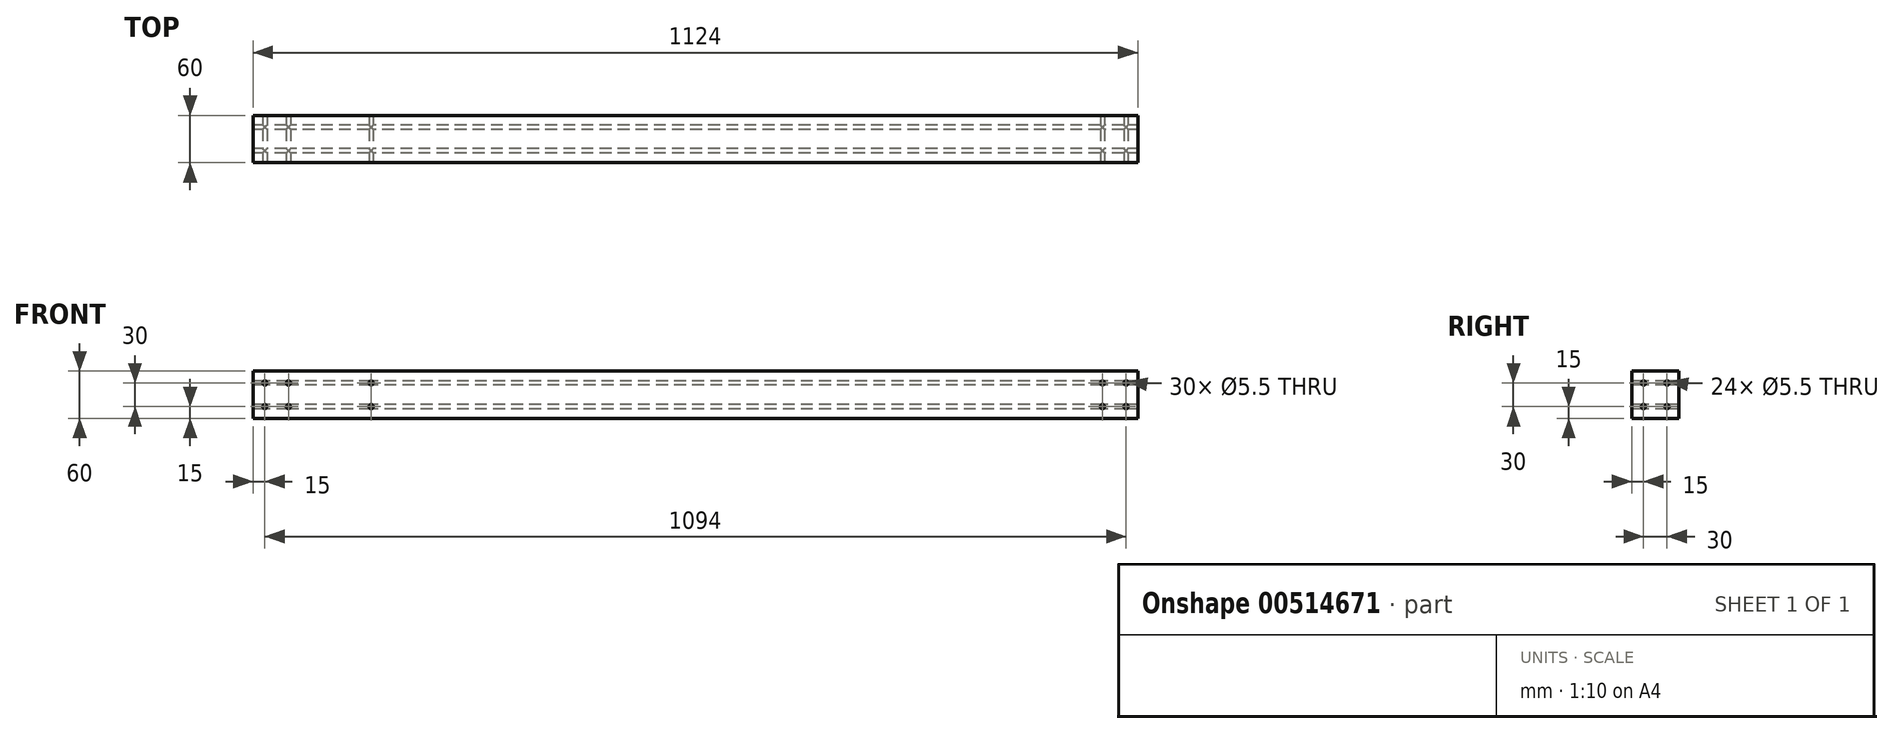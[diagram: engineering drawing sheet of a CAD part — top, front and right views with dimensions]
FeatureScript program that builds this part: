
annotation { "Feature Type Name" : "Feature", "Feature Type Description" : "" }
export const myFeature = defineFeature(function(context is Context, id is Id, definition is map)
    precondition{}
    {
        {
            var Q0;
            Q0=qCreatedBy(makeId("Right.planeOp"),FACE);
            var sketch = newSketch(context, id + "F0", { "sketchPlane" : qUnion([Q0])});
            skLineSegment(sketch, "E0.bottom", {"start": v(0, 0) * mm, "end": v(-60, 0) * mm});
            skLineSegment(sketch, "E0.top", {"start": v(0, 60) * mm, "end": v(-60, 60) * mm});
            skLineSegment(sketch, "E0.left", {"start": v(0, 0) * mm, "end": v(0, 60) * mm});
            skLineSegment(sketch, "E0.right", {"start": v(-60, 0) * mm, "end": v(-60, 60) * mm});
            skPoint(sketch, "E1", {"position": v(-45, 45) * mm});
            skPoint(sketch, "E2", {"position": v(-45, 15) * mm});
            skPoint(sketch, "E3", {"position": v(-15, 15) * mm});
            skPoint(sketch, "E4", {"position": v(-15, 45) * mm});
            skSolve(sketch);
        }
        {
            var Q0;
            Q0=makeQuery(id+"F0.imprint","IMPRINT",FACE,{"disambiguationData":[TD([[makeQuery(id+"F0.imprint","IMPRINT",EDGE,{"derivedFrom":sQuery(id+"F0.wireOp",EDGE,"E0.bottom")}),-1.0]])]});
            extrude(context, id + "F1", {"entities" : qUnion([Q0]), "depth" : 1124 * mm, "offsetDistance" : 25 * mm});
        }
        {
            var Q0;
            Q0=sQuery(id+"F0.wireOp",VERTEX,"E1");
            var Q1;
            Q1=sQuery(id+"F0.wireOp",VERTEX,"E2");
            var Q2;
            Q2=sQuery(id+"F0.wireOp",VERTEX,"E3");
            var Q3;
            Q3=sQuery(id+"F0.wireOp",VERTEX,"E4");
            var Q4;
            Q4=makeQuery(id+"F1.opExtrude","SWEPT_BODY",BODY,{"disambiguationData":[OSD([sQuery(id+"F0.wireOp",EDGE,"E0.bottom"),sQuery(id+"F0.wireOp",EDGE,"E0.top"),sQuery(id+"F0.wireOp",EDGE,"E0.left"),sQuery(id+"F0.wireOp",EDGE,"E0.right")])]});
            hole(context, id + "F2", {"style" : HoleStyle.SIMPLE, "endStyle" : HoleEndStyle.THROUGH, "oppositeDirection" : true, "standardTappedOrClearance" : lookupTablePath({ "standard" : "ISO", "fit" : "Normal", "size" : "M5", "type" : "Clearance" }), "standardBlindInLast" : lookupTablePath({ "fit" : "Standard", "standard" : "ISO", "size" : "M5", "type" : "Clearance" }), "holeDiameter" : 5.5 * mm, "isTappedThrough" : true, "tappedDepth" : 12 * mm, "tapClearance" : 3, "locations" : qUnion([Q0, Q1, Q2, Q3]), "scope" : qUnion([Q4])});
        }
        {
            var Q0;
            Q0=makeQuery(id+"F1.opExtrude","SWEPT_FACE",FACE,{"disambiguationData":[OSD([sQuery(id+"F0.wireOp",EDGE,"E0.right")])]});
            var sketch = newSketch(context, id + "F3", { "sketchPlane" : qUnion([Q0])});
            skPoint(sketch, "E5", {"position": v(150, 45) * mm});
            skPoint(sketch, "E6", {"position": v(150, 15) * mm});
            skPoint(sketch, "E7", {"position": v(15, 45) * mm});
            skPoint(sketch, "E8", {"position": v(45, 45) * mm});
            skPoint(sketch, "E9", {"position": v(45, 15) * mm});
            skPoint(sketch, "E10", {"position": v(15, 15) * mm});
            skPoint(sketch, "E11", {"position": v(1079, 45) * mm});
            skPoint(sketch, "E12", {"position": v(1109, 45) * mm});
            skPoint(sketch, "E13", {"position": v(1109, 15) * mm});
            skPoint(sketch, "E14", {"position": v(1079, 15) * mm});
            skSolve(sketch);
        }
        {
            var Q0;
            Q0=sQuery(id+"F3.wireOp",VERTEX,"E5");
            var Q1;
            Q1=sQuery(id+"F3.wireOp",VERTEX,"E6");
            var Q2;
            Q2=makeQuery(id+"F1.opExtrude","SWEPT_BODY",BODY,{"disambiguationData":[OSD([sQuery(id+"F0.wireOp",EDGE,"E0.bottom"),sQuery(id+"F0.wireOp",EDGE,"E0.top"),sQuery(id+"F0.wireOp",EDGE,"E0.left"),sQuery(id+"F0.wireOp",EDGE,"E0.right")])]});
            hole(context, id + "F4", {"style" : HoleStyle.SIMPLE, "endStyle" : HoleEndStyle.THROUGH, "standardTappedOrClearance" : lookupTablePath({ "standard" : "ISO", "fit" : "Normal", "size" : "M5", "type" : "Clearance" }), "standardBlindInLast" : lookupTablePath({ "fit" : "Standard", "standard" : "ISO", "size" : "M5", "type" : "Clearance" }), "holeDiameter" : 5.5 * mm, "isTappedThrough" : true, "tappedDepth" : 12 * mm, "tapClearance" : 3, "locations" : qUnion([Q0, Q1]), "scope" : qUnion([Q2])});
        }
        {
            var Q0;
            Q0=sQuery(id+"F3.wireOp",VERTEX,"E8");
            var Q1;
            Q1=sQuery(id+"F3.wireOp",VERTEX,"E7");
            var Q2;
            Q2=sQuery(id+"F3.wireOp",VERTEX,"E10");
            var Q3;
            Q3=sQuery(id+"F3.wireOp",VERTEX,"E9");
            var Q4;
            Q4=sQuery(id+"F3.wireOp",VERTEX,"E12");
            var Q5;
            Q5=sQuery(id+"F3.wireOp",VERTEX,"E14");
            var Q6;
            Q6=sQuery(id+"F3.wireOp",VERTEX,"E13");
            var Q7;
            Q7=sQuery(id+"F3.wireOp",VERTEX,"E11");
            var Q8;
            Q8=makeQuery(id+"F1.opExtrude","SWEPT_BODY",BODY,{"disambiguationData":[OSD([sQuery(id+"F0.wireOp",EDGE,"E0.bottom"),sQuery(id+"F0.wireOp",EDGE,"E0.top"),sQuery(id+"F0.wireOp",EDGE,"E0.left"),sQuery(id+"F0.wireOp",EDGE,"E0.right")])]});
            hole(context, id + "F5", {"style" : HoleStyle.SIMPLE, "endStyle" : HoleEndStyle.THROUGH, "standardTappedOrClearance" : lookupTablePath({ "standard" : "ISO", "fit" : "Normal", "size" : "M5", "type" : "Clearance" }), "standardBlindInLast" : lookupTablePath({ "fit" : "Standard", "standard" : "ISO", "size" : "M5", "type" : "Clearance" }), "holeDiameter" : 5.5 * mm, "isTappedThrough" : true, "tappedDepth" : 12 * mm, "tapClearance" : 3, "locations" : qUnion([Q0, Q1, Q2, Q3, Q4, Q5, Q6, Q7]), "scope" : qUnion([Q8])});
        }
    });
